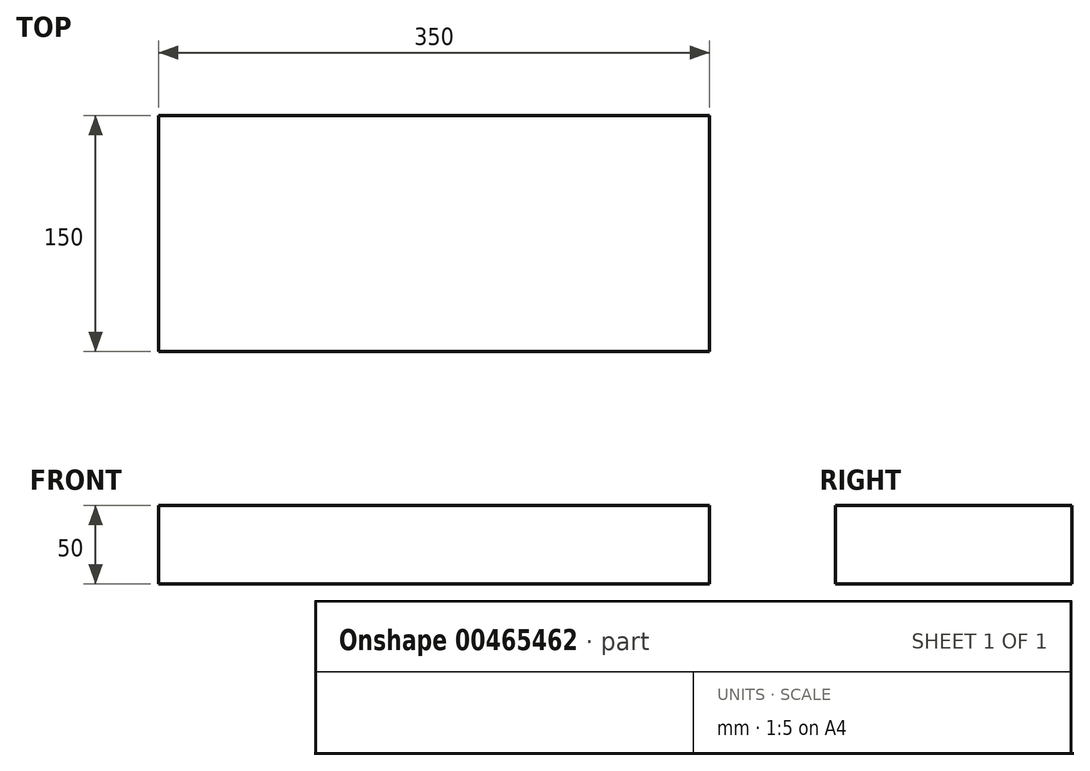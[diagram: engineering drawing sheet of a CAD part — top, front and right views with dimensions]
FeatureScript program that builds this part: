
annotation { "Feature Type Name" : "Feature", "Feature Type Description" : "" }
export const myFeature = defineFeature(function(context is Context, id is Id, definition is map)
    precondition{}
    {
        {
            var Q0;
            Q0=qCreatedBy(makeId("Top.planeOp"),FACE);
            var sketch = newSketch(context, id + "F0", { "sketchPlane" : qUnion([Q0])});
            skLineSegment(sketch, "E0.bottom", {"start": v(-509.87, -280.53) * mm, "end": v(-159.87, -280.53) * mm});
            skLineSegment(sketch, "E0.top", {"start": v(-509.87, -130.53) * mm, "end": v(-159.87, -130.53) * mm});
            skLineSegment(sketch, "E0.left", {"start": v(-509.87, -280.53) * mm, "end": v(-509.87, -130.53) * mm});
            skLineSegment(sketch, "E0.right", {"start": v(-159.87, -280.53) * mm, "end": v(-159.87, -130.53) * mm});
            skSolve(sketch);
        }
        {
            var Q0;
            Q0=qSketchRegion(id+"F0",true);
            extrude(context, id + "F1", {"entities" : qUnion([Q0]), "depth" : 50 * mm});
        }
    });
